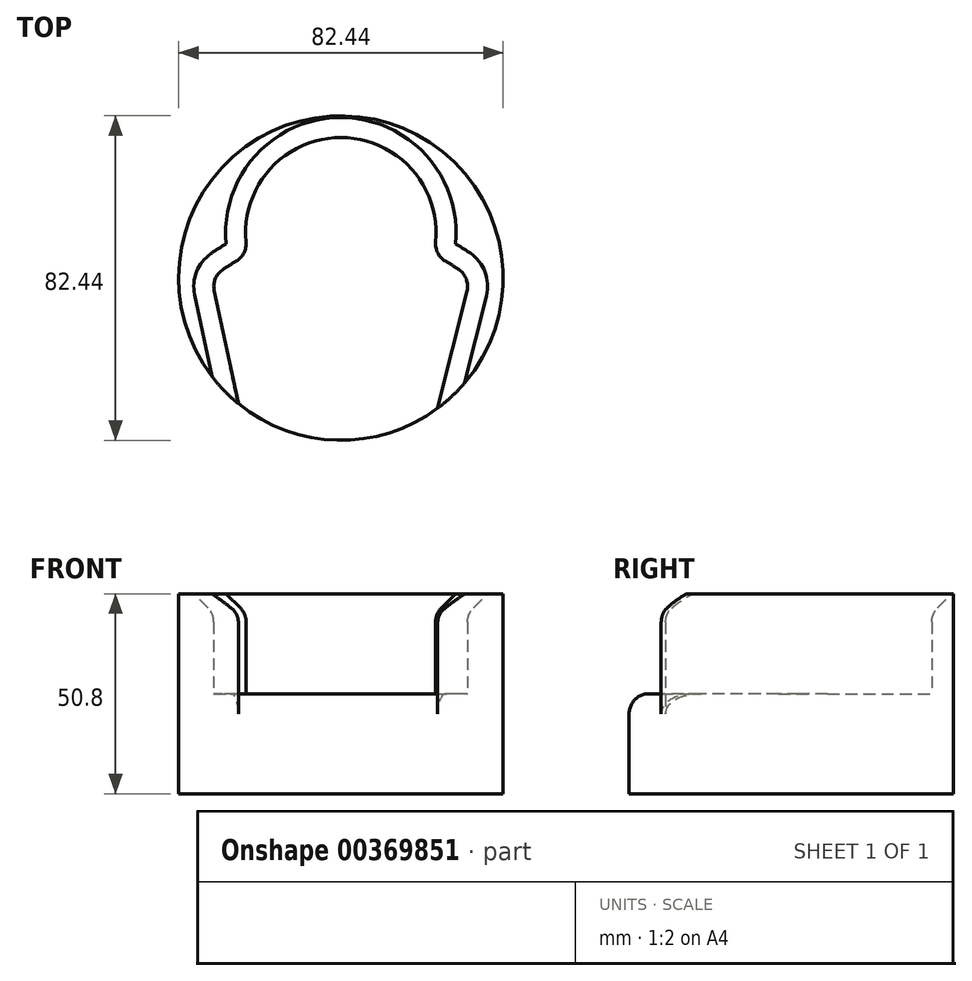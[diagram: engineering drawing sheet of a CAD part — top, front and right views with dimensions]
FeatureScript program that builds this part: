
annotation { "Feature Type Name" : "Feature", "Feature Type Description" : "" }
export const myFeature = defineFeature(function(context is Context, id is Id, definition is map)
    precondition{}
    {
        {
            var Q0;
            Q0=qCreatedBy(makeId("Top.planeOp"),FACE);
            var sketch = newSketch(context, id + "F0", { "sketchPlane" : qUnion([Q0])});
            skCircle(sketch, "E0", {"center": v(0, 0) * mm, "radius": 41.22 * mm});
            skArc(sketch, "E1", {"start": v(32.85, 0) * mm, "mid": v(28.36, 3.21) * mm, "end": v(23.55, 5.94) * mm});
            skArc(sketch, "E2", {"start": v(23.55, 5.94) * mm, "mid": v(0, 35.69) * mm, "end": v(-23.55, 5.94) * mm});
            skLineSegment(sketch, "E3", {"start": v(32.85, 0) * mm, "end": v(24.61, -33.06) * mm});
            skLineSegment(sketch, "E4", {"start": v(-32.85, 0) * mm, "end": v(-26.06, -31.93) * mm});
            skArc(sketch, "E5.trimOffspring", {"start": v(-23.55, 5.94) * mm, "mid": v(-28.36, 3.21) * mm, "end": v(-32.85, 0) * mm});
            skSolve(sketch);
        }
        {
            var Q0;
            Q0=makeQuery(id+"F0.imprint","IMPRINT",FACE,{"disambiguationData":[TD([[makeQuery(id+"F0.imprint","IMPRINT",EDGE,{"derivedFrom":sQuery(id+"F0.wireOp",EDGE,"E1")}),1.0]])]});
            extrude(context, id + "F1", {"entities" : qUnion([Q0]), "depth" : 25.4 * mm});
        }
        {
            var Q0;
            Q0=makeQuery(id+"F0.imprint","IMPRINT",FACE,{"disambiguationData":[TD([[makeQuery(id+"F0.imprint","IMPRINT",EDGE,{"derivedFrom":sQuery(id+"F0.wireOp",EDGE,"E1")}),-1.0]])]});
            extrude(context, id + "F2", {"entities" : qUnion([Q0]), "operationType" : NewBodyOperationType.ADD, "depth" : 50.8 * mm});
        }
        {
            var Q0;
            Q0=makeQuery(id+"F2.opExtrude","SWEPT_EDGE",EDGE,{"disambiguationData":[OSD([sQuery(id+"F0.wireOp",EDGE,"E4"),sQuery(id+"F0.wireOp",EDGE,"E5.trimOffspring")])]});
            var Q1;
            Q1=makeQuery(id+"F2.opExtrude","SWEPT_EDGE",EDGE,{"disambiguationData":[OSD([sQuery(id+"F0.wireOp",EDGE,"E2"),sQuery(id+"F0.wireOp",EDGE,"E5.trimOffspring")])]});
            var Q2;
            Q2=makeQuery(id+"F2.opExtrude","SWEPT_EDGE",EDGE,{"disambiguationData":[OSD([sQuery(id+"F0.wireOp",EDGE,"E1"),sQuery(id+"F0.wireOp",EDGE,"E2")])]});
            var Q3;
            Q3=makeQuery(id+"F2.opExtrude","SWEPT_EDGE",EDGE,{"disambiguationData":[OSD([sQuery(id+"F0.wireOp",EDGE,"E1"),sQuery(id+"F0.wireOp",EDGE,"E3")])]});
            fillet(context, id + "F3", {"entities" : qUnion([Q0, Q1, Q2, Q3]), "radius" : 5.08 * mm, "tangentPropagation" : true, "allowEdgeOverflow" : false});
        }
        {
            var Q0;
            Q0=makeQuery(id+"F2.opExtrude","CAP_EDGE",EDGE,{"disambiguationData":[OSD([sQuery(id+"F0.wireOp",EDGE,"E4")])],"isStart":false});
            chamfer(context, id + "F4", {"entities" : qUnion([Q0]), "width" : 5.08 * mm, "tangentPropagation" : true});
        }
        {
            var Q0;
            {var subQ0=sQuery(id+"F0.wireOp",EDGE,"E2");Q0=makeQuery(id+"F4.opChamfer","BLEND_EDGE",EDGE,{"blendedFrom":[makeQuery(id+"F2.opExtrude","CAP_EDGE",EDGE,{"disambiguationData":[OSD([subQ0])],"isStart":false}),makeQuery(id+"F2.opExtrude","SWEPT_FACE",FACE,{"disambiguationData":[OSD([subQ0])]})],"blendedInto":[makeQuery(id+"F2.opExtrude","SWEPT_FACE",FACE,{"disambiguationData":[OSD([subQ0])]})]});}
            fillet(context, id + "F5", {"entities" : qUnion([Q0]), "radius" : 5.08 * mm, "tangentPropagation" : true, "allowEdgeOverflow" : false});
        }
        {
            var Q0;
            Q0=makeQuery(id+"F1.opExtrude","CAP_EDGE",EDGE,{"disambiguationData":[OSD([sQuery(id+"F0.wireOp",EDGE,"E0")])],"isStart":false});
            fillet(context, id + "F6", {"entities" : qUnion([Q0]), "radius" : 5.08 * mm, "tangentPropagation" : true, "allowEdgeOverflow" : false});
        }
    });
